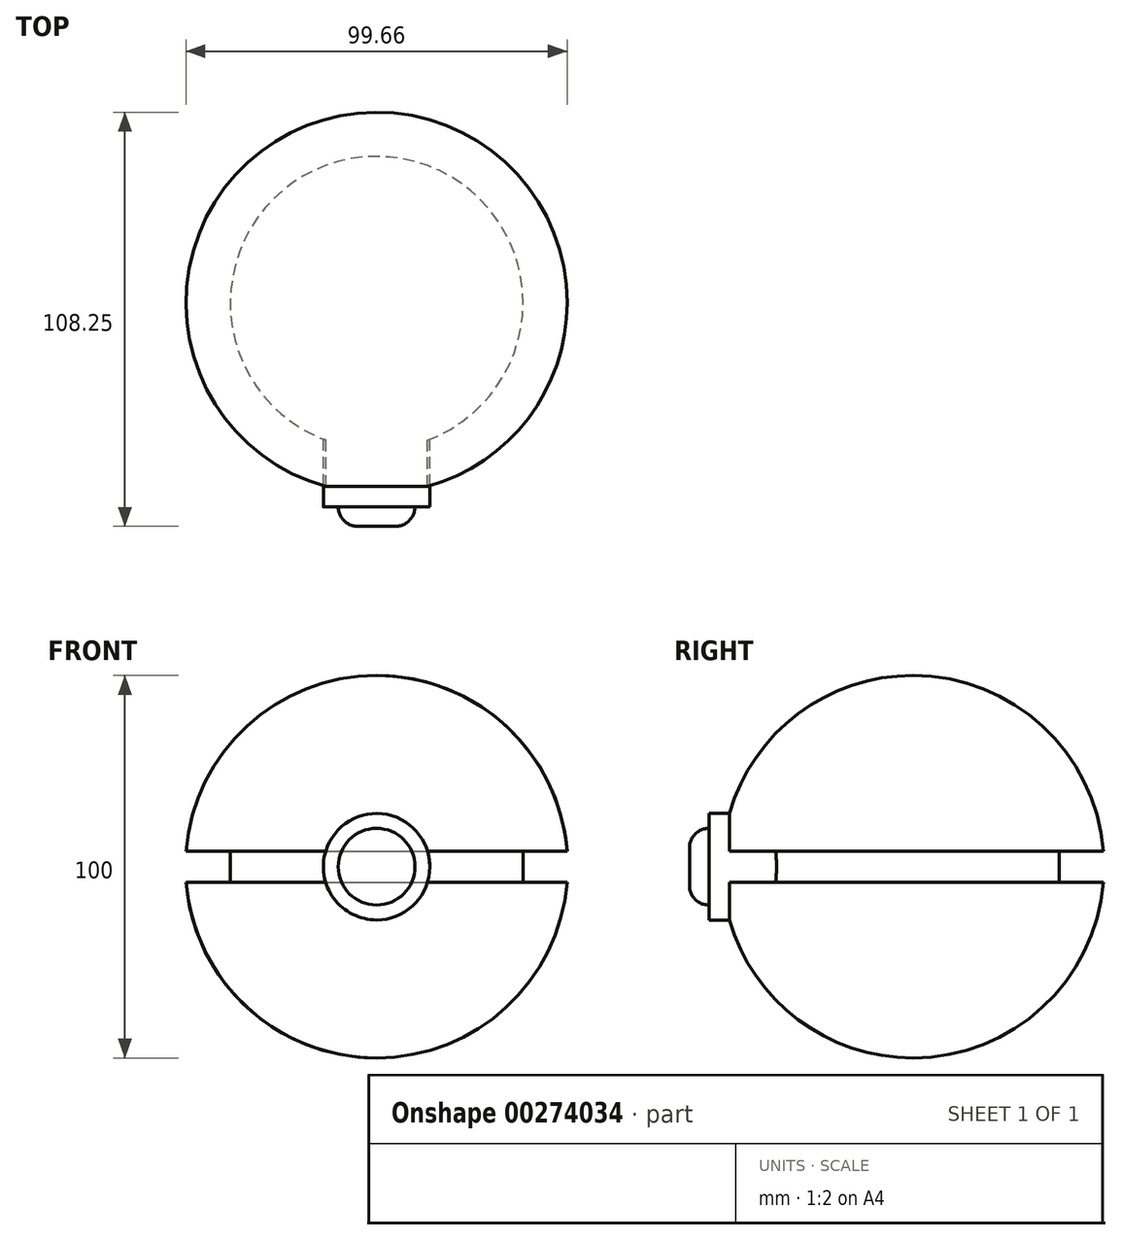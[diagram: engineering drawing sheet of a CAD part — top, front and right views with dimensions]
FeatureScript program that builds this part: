
annotation { "Feature Type Name" : "Feature", "Feature Type Description" : "" }
export const myFeature = defineFeature(function(context is Context, id is Id, definition is map)
    precondition{}
    {
        {
            var Q0;
            Q0=qCreatedBy(makeId("Front.planeOp"),FACE);
            var sketch = newSketch(context, id + "F0", { "sketchPlane" : qUnion([Q0])});
            skArc(sketch, "E0", {"start": v(0, -50) * mm, "mid": v(33.88, -36.77) * mm, "end": v(49.83, -4.1) * mm});
            skLineSegment(sketch, "E1", {"start": v(0, 0) * mm, "end": v(0, 50) * mm});
            skLineSegment(sketch, "E2", {"start": v(0, 0) * mm, "end": v(0, -50) * mm});
            skLineSegment(sketch, "E3", {"start": v(49.83, 4.1) * mm, "end": v(38.28, 4.1) * mm});
            skLineSegment(sketch, "E4", {"start": v(38.28, 4.1) * mm, "end": v(38.28, 0) * mm});
            skLineSegment(sketch, "E5", {"start": v(38.28, 0) * mm, "end": v(50, 0) * mm, "construction": true});
            skLineSegment(sketch, "E6.MirrorCS", {"start": v(49.32, 8.19) * mm, "end": v(50, 8.19) * mm, "construction": true});
            skLineSegment(sketch, "E7.MirrorCS", {"start": v(38.28, -4.1) * mm, "end": v(38.28, 0) * mm});
            skLineSegment(sketch, "E8.MirrorCS", {"start": v(49.83, -4.1) * mm, "end": v(38.28, -4.1) * mm});
            skPoint(sketch, "E9.orphan", {"position": v(38.28, 8.19) * mm});
            skArc(sketch, "E10.trimOffspring", {"start": v(49.83, 4.1) * mm, "mid": v(33.88, 36.77) * mm, "end": v(0, 50) * mm});
            skSolve(sketch);
        }
        {
            var Q0;
            Q0=makeQuery(id+"F0.imprint","IMPRINT",FACE,{"disambiguationData":[TD([[makeQuery(id+"F0.imprint","IMPRINT",EDGE,{"derivedFrom":sQuery(id+"F0.wireOp",EDGE,"E0")}),1.0]])]});
            var Q1;
            Q1=sQuery(id+"F0.wireOp",EDGE,"E1");
            revolve(context, id + "F1", {"entities" : qUnion([Q0]), "axis" : qUnion([Q1]), "revolveType" : RevolveType.FULL});
        }
        {
            var Q0;
            Q0=qCreatedBy(makeId("Front.planeOp"),FACE);
            var sketch = newSketch(context, id + "F2", { "sketchPlane" : qUnion([Q0])});
            skCircle(sketch, "E11", {"center": v(0, 0) * mm, "radius": 13.92 * mm});
            skSolve(sketch);
        }
        {
            var Q0;
            Q0 = qSketchRegion(id + "F2", true);
            extrude(context, id + "F3", {"entities" : qUnion([Q0]), "operationType" : NewBodyOperationType.ADD, "depth" : 53.34 * mm});
        }
        {
            var Q0;
            Q0=makeQuery(id+"F3.opExtrude","CAP_FACE",FACE,{"disambiguationData":[OSD([sQuery(id+"F2.wireOp",EDGE,"E11")])],"isStart":false});
            var sketch = newSketch(context, id + "F4", { "sketchPlane" : qUnion([Q0])});
            skCircle(sketch, "E12", {"center": v(0, 0) * mm, "radius": 10.03 * mm});
            skSolve(sketch);
        }
        {
            var Q0;
            Q0 = qSketchRegion(id + "F4", true);
            extrude(context, id + "F5", {"entities" : qUnion([Q0]), "operationType" : NewBodyOperationType.ADD, "depth" : 5.08 * mm});
        }
        {
            var Q0;
            Q0=makeQuery(id+"F5.opExtrude","CAP_FACE",FACE,{"disambiguationData":[OSD([sQuery(id+"F4.wireOp",EDGE,"E12")])],"isStart":false});
            fillet(context, id + "F6", {"entities" : qUnion([Q0]), "radius" : 5.08 * mm, "tangentPropagation" : true, "allowEdgeOverflow" : false});
        }
    });
